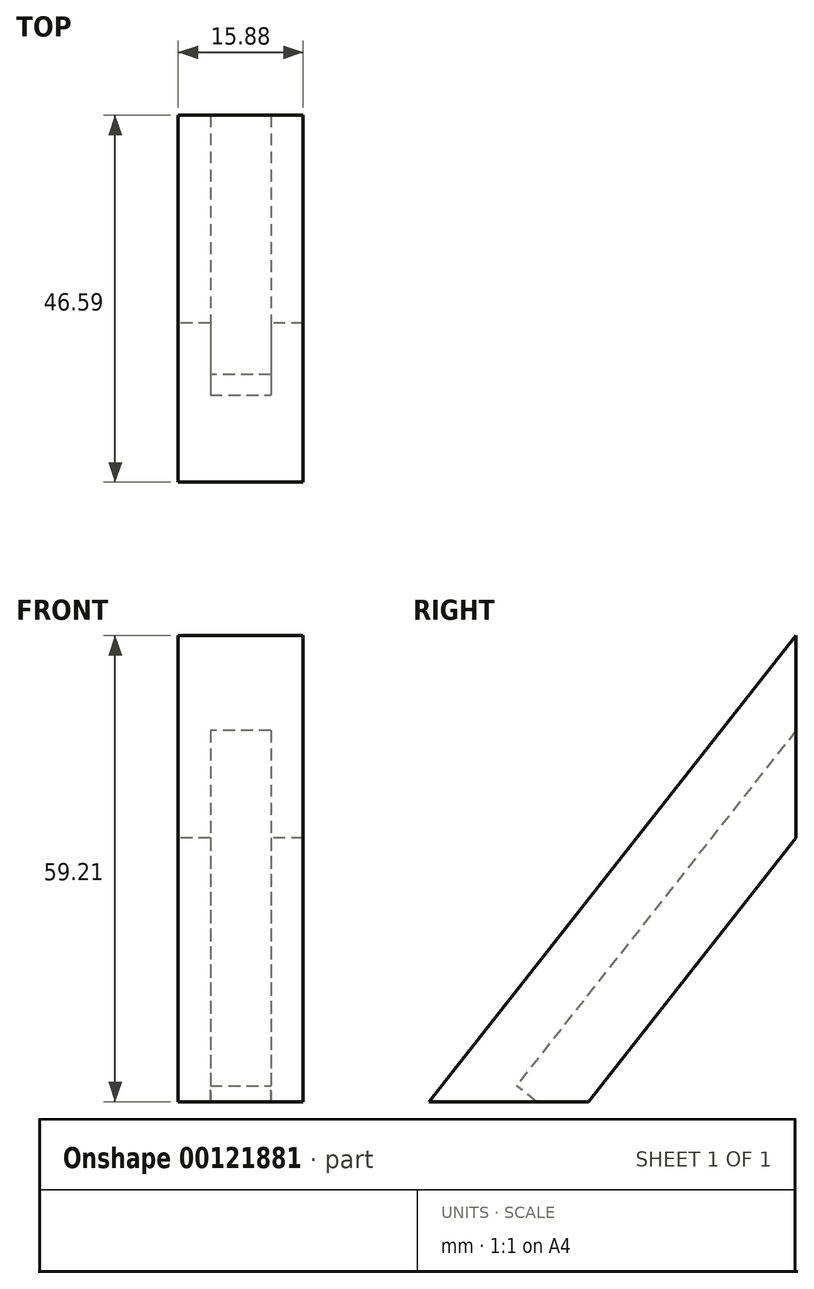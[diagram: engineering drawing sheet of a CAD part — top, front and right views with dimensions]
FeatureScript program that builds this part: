
annotation { "Feature Type Name" : "Feature", "Feature Type Description" : "" }
export const myFeature = defineFeature(function(context is Context, id is Id, definition is map)
    precondition{}
    {
        {
            var Q0;
            Q0=qCreatedBy(makeId("Right.planeOp"),FACE);
            var sketch = newSketch(context, id + "F0", { "sketchPlane" : qUnion([Q0])});
            skSolve(sketch);
        }
        {
            var Q0;
            Q0=qCreatedBy(makeId("Right.planeOp"),FACE);
            var sketch = newSketch(context, id + "F6", { "sketchPlane" : qUnion([Q0])});
            skLineSegment(sketch, "E0", {"start": v(0, 0) * mm, "end": v(20.2, 0) * mm});
            skLineSegment(sketch, "E1", {"start": v(20.2, 0) * mm, "end": v(46.59, 33.53) * mm});
            skLineSegment(sketch, "E2", {"start": v(46.59, 33.53) * mm, "end": v(46.59, 59.2) * mm});
            skLineSegment(sketch, "E3", {"start": v(46.59, 59.2) * mm, "end": v(0, 0) * mm});
            skSolve(sketch);
        }
        {
            var Q0;
            Q0 = qSketchRegion(id + "F0", true);
            var Q1;
            Q1=makeQuery(id+"F6.imprint","IMPRINT",FACE,{"disambiguationData":[TD([[makeQuery(id+"F6.imprint","IMPRINT",EDGE,{"derivedFrom":sQuery(id+"F6.wireOp",EDGE,"E0")}),1.0]])]});
            extrude(context, id + "F1", {"entities" : qUnion([Q0, Q1]), "endBound" : BoundingType.SYMMETRIC, "depth" : 15.88 * mm});
        }
        {
            var Q0;
            Q0=makeQuery(id+"F1.opExtrude","CAP_FACE",FACE,{"disambiguationData":[OSD([sQuery(id+"F6.wireOp",EDGE,"E0"),sQuery(id+"F6.wireOp",EDGE,"E1"),sQuery(id+"F6.wireOp",EDGE,"E2"),sQuery(id+"F6.wireOp",EDGE,"E3")])],"isStart":false});
            var sketch = newSketch(context, id + "F2", { "sketchPlane" : qUnion([Q0])});
            skLineSegment(sketch, "E4", {"start": v(33.4, 16.77) * mm, "end": v(20.92, 26.58) * mm, "construction": true});
            skSolve(sketch);
        }
        {
            var Q0;
            Q0=sQuery(id+"F2.wireOp",EDGE,"E4");
            cPlane(context, id + "F3", {"entities" : qUnion([Q0]), "cplaneType" : CPlaneType.LINE_ANGLE, "offset" : 25.4 * mm, "angle" : 0 * degree, "width" : 152.4 * mm, "height" : 152.4 * mm});
        }
        {
            var Q0;
            Q0=qCreatedBy(id+"F3.planeOp",FACE);
            var sketch = newSketch(context, id + "F4", { "sketchPlane" : qUnion([Q0])});
            skLineSegment(sketch, "E5.top", {"start": v(-3.85, -7.45) * mm, "end": v(3.85, -7.45) * mm});
            skLineSegment(sketch, "E5.left", {"start": v(-3.85, -16.29) * mm, "end": v(-3.85, -7.45) * mm});
            skLineSegment(sketch, "E5.right", {"start": v(3.85, -16.29) * mm, "end": v(3.85, -7.45) * mm});
            skPoint(sketch, "E5.middle", {"position": v(0, -11.87) * mm});
            skLineSegment(sketch, "E6", {"start": v(3.85, -16.29) * mm, "end": v(-3.85, -16.29) * mm});
            skSolve(sketch);
        }
        {
            var Q0;
            Q0 = qSketchRegion(id + "F4", true);
            extrude(context, id + "F5", {"entities" : qUnion([Q0]), "operationType" : NewBodyOperationType.REMOVE, "endBound" : BoundingType.UP_TO_NEXT, "oppositeDirection" : true, "depth" : 152.4 * mm, "hasSecondDirection" : true, "secondDirectionOppositeDirection" : false, "secondDirectionDepth" : 25.4 * mm});
        }
    });
